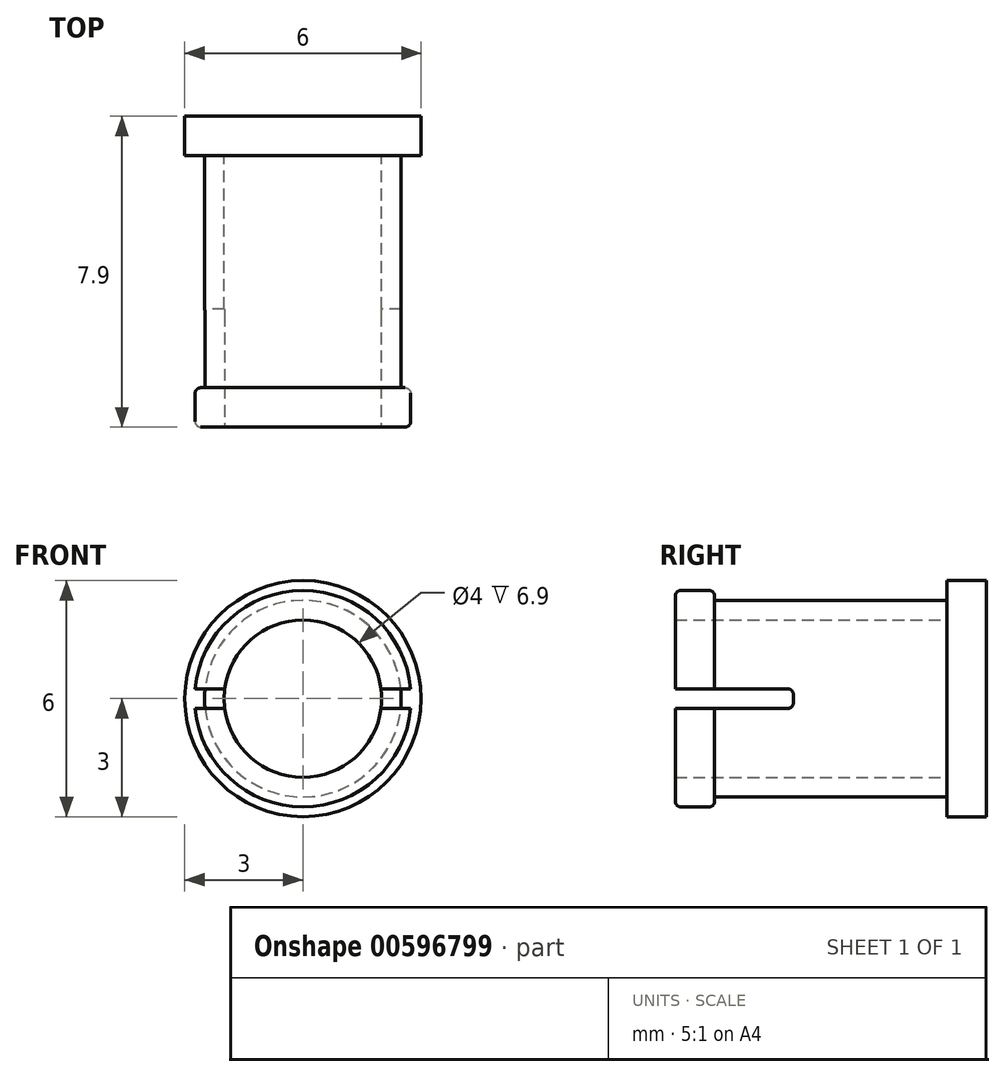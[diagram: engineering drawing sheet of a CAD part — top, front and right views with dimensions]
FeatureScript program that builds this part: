
annotation { "Feature Type Name" : "Feature", "Feature Type Description" : "" }
export const myFeature = defineFeature(function(context is Context, id is Id, definition is map)
    precondition{}
    {
        {
            var Q0;
            Q0=qCreatedBy(makeId("Front.planeOp"),FACE);
            var sketch = newSketch(context, id + "F0", { "sketchPlane" : qUnion([Q0])});
            skCircle(sketch, "E0", {"center": v(0, 0) * mm, "radius": 3 * mm});
            skSolve(sketch);
        }
        {
            var Q0;
            Q0=qSketchRegion(id+"F0",true);
            extrude(context, id + "F1", {"entities" : qUnion([Q0]), "endBound" : BoundingType.SYMMETRIC, "depth" : 1 * mm, "offsetDistance" : 25 * mm});
        }
        {
            var Q0;
            Q0=makeQuery(id+"F1.opExtrude","CAP_FACE",FACE,{"disambiguationData":[OSD([sQuery(id+"F0.wireOp",EDGE,"E0")])],"isStart":false});
            var sketch = newSketch(context, id + "F2", { "sketchPlane" : qUnion([Q0])});
            skCircle(sketch, "E1", {"center": v(0, 0) * mm, "radius": 2.5 * mm});
            skCircle(sketch, "E2", {"center": v(0, 0) * mm, "radius": 2 * mm});
            skSolve(sketch);
        }
        {
            var Q0;
            Q0=makeQuery(id+"F2.imprint","IMPRINT",FACE,{"disambiguationData":[TD([[makeQuery(id+"F2.imprint","IMPRINT",EDGE,{"derivedFrom":sQuery(id+"F2.wireOp",EDGE,"E1")}),1.0]])]});
            extrude(context, id + "F3", {"entities" : qUnion([Q0]), "operationType" : NewBodyOperationType.ADD, "depth" : 5.9 * mm, "offsetDistance" : 25 * mm});
        }
        {
            var Q0;
            Q0=makeQuery(id+"F3.opExtrude","CAP_FACE",FACE,{"disambiguationData":[OSD([sQuery(id+"F2.wireOp",EDGE,"E1"),sQuery(id+"F2.wireOp",EDGE,"E2")])],"isStart":false});
            var sketch = newSketch(context, id + "F4", { "sketchPlane" : qUnion([Q0])});
            skCircle(sketch, "E3", {"center": v(0, 0) * mm, "radius": 2.75 * mm});
            skCircle(sketch, "E4", {"center": v(0, 0) * mm, "radius": 2 * mm});
            skSolve(sketch);
        }
        {
            var Q0;
            Q0=qSketchRegion(id+"F4",true);
            extrude(context, id + "F5", {"entities" : qUnion([Q0]), "operationType" : NewBodyOperationType.ADD, "depth" : 1 * mm, "offsetDistance" : 25 * mm});
        }
        {
            var Q0;
            Q0=makeQuery(id+"F5.opExtrude","CAP_FACE",FACE,{"disambiguationData":[OSD([sQuery(id+"F4.wireOp",EDGE,"E3"),sQuery(id+"F4.wireOp",EDGE,"E4")])],"isStart":false});
            var sketch = newSketch(context, id + "F6", { "sketchPlane" : qUnion([Q0])});
            skLineSegment(sketch, "E5.bottom", {"start": v(2.74, 0.25) * mm, "end": v(1.98, 0.25) * mm});
            skLineSegment(sketch, "E5.top", {"start": v(2.74, -0.25) * mm, "end": v(1.98, -0.25) * mm});
            skPoint(sketch, "E5.middle", {"position": v(0, 0) * mm});
            skArc(sketch, "E6.0", {"start": v(1.98, -0.25) * mm, "mid": v(2, 0) * mm, "end": v(1.98, 0.25) * mm});
            skArc(sketch, "E7.0", {"start": v(2.74, -0.25) * mm, "mid": v(2.75, 0) * mm, "end": v(2.74, 0.25) * mm});
            skPoint(sketch, "E5.right.start.orphan", {"position": v(-3.56, 0.25) * mm});
            skPoint(sketch, "E8.orphan", {"position": v(-3.56, -0.25) * mm});
            skLineSegment(sketch, "E9.trimOffspring", {"start": v(-1.98, -0.25) * mm, "end": v(-2.74, -0.25) * mm});
            skLineSegment(sketch, "E10.trimOffspring", {"start": v(-1.98, 0.25) * mm, "end": v(-2.74, 0.25) * mm});
            skArc(sketch, "E11.trimOffspring", {"start": v(-1.98, 0.25) * mm, "mid": v(-2, 0) * mm, "end": v(-1.98, -0.25) * mm});
            skArc(sketch, "E12.trimOffspring", {"start": v(-2.74, 0.25) * mm, "mid": v(-2.75, 0) * mm, "end": v(-2.74, -0.25) * mm});
            skPoint(sketch, "E5.left.start.orphan", {"position": v(3.56, 0.25) * mm});
            skPoint(sketch, "E13.orphan", {"position": v(3.56, -0.25) * mm});
            skSolve(sketch);
        }
        {
            var Q0;
            Q0=qSketchRegion(id+"F6",true);
            extrude(context, id + "F7", {"entities" : qUnion([Q0]), "operationType" : NewBodyOperationType.REMOVE, "oppositeDirection" : true, "depth" : 3 * mm, "offsetDistance" : 25 * mm});
        }
        {
            var Q0;
            Q0=makeQuery(id+"F7.boolean.opBoolean","COPY",EDGE,{"derivedFrom":makeQuery(id+"F7.opExtrude","CAP_EDGE",EDGE,{"disambiguationData":[OSD([sQuery(id+"F6.wireOp",EDGE,"E9.trimOffspring")])],"isStart":false})});
            var Q1;
            {var subQ0=sQuery(id+"F4.wireOp",EDGE,"E3");Q1=makeQuery(id+"F7.boolean.opBoolean","SPLIT",EDGE,{"disambiguationData":[TD([makeQuery(id+"F7.opExtrude","SWEPT_FACE",FACE,{"disambiguationData":[OSD([sQuery(id+"F6.wireOp",EDGE,"E5.bottom")])]})])],"derivedFrom":makeQuery(id+"F5.opExtrude","CAP_EDGE",EDGE,{"disambiguationData":[OSD([subQ0])],"isStart":true})});}
            var Q2;
            {var subQ0=sQuery(id+"F4.wireOp",EDGE,"E3");Q2=makeQuery(id+"F7.boolean.opBoolean","SPLIT",EDGE,{"disambiguationData":[TD([makeQuery(id+"F7.opExtrude","SWEPT_FACE",FACE,{"disambiguationData":[OSD([sQuery(id+"F6.wireOp",EDGE,"E5.bottom")])]})])],"derivedFrom":makeQuery(id+"F5.opExtrude","CAP_EDGE",EDGE,{"disambiguationData":[OSD([subQ0])],"isStart":false})});}
            var Q3;
            {var subQ0=sQuery(id+"F4.wireOp",EDGE,"E3");Q3=makeQuery(id+"F7.boolean.opBoolean","SPLIT",EDGE,{"disambiguationData":[TD([makeQuery(id+"F7.opExtrude","SWEPT_FACE",FACE,{"disambiguationData":[OSD([sQuery(id+"F6.wireOp",EDGE,"E5.top")])]})])],"derivedFrom":makeQuery(id+"F5.opExtrude","CAP_EDGE",EDGE,{"disambiguationData":[OSD([subQ0])],"isStart":false})});}
            var Q4;
            {var subQ0=sQuery(id+"F4.wireOp",EDGE,"E3");Q4=makeQuery(id+"F7.boolean.opBoolean","SPLIT",EDGE,{"disambiguationData":[TD([makeQuery(id+"F7.opExtrude","SWEPT_FACE",FACE,{"disambiguationData":[OSD([sQuery(id+"F6.wireOp",EDGE,"E5.top")])]})])],"derivedFrom":makeQuery(id+"F5.opExtrude","CAP_EDGE",EDGE,{"disambiguationData":[OSD([subQ0])],"isStart":true})});}
            var Q5;
            Q5=makeQuery(id+"F7.boolean.opBoolean","COPY",EDGE,{"derivedFrom":makeQuery(id+"F7.opExtrude","CAP_EDGE",EDGE,{"disambiguationData":[OSD([sQuery(id+"F6.wireOp",EDGE,"E5.top")])],"isStart":false})});
            var Q6;
            Q6=makeQuery(id+"F7.boolean.opBoolean","COPY",EDGE,{"derivedFrom":makeQuery(id+"F7.opExtrude","CAP_EDGE",EDGE,{"disambiguationData":[OSD([sQuery(id+"F6.wireOp",EDGE,"E5.bottom")])],"isStart":false})});
            var Q7;
            Q7=makeQuery(id+"F7.boolean.opBoolean","COPY",EDGE,{"derivedFrom":makeQuery(id+"F7.opExtrude","CAP_EDGE",EDGE,{"disambiguationData":[OSD([sQuery(id+"F6.wireOp",EDGE,"E10.trimOffspring")])],"isStart":false})});
            fillet(context, id + "F8", {"entities" : qUnion([Q0, Q1, Q2, Q3, Q4, Q5, Q6, Q7]), "radius" : 0.14 * mm, "tangentPropagation" : true, "allowEdgeOverflow" : false});
        }
    });
